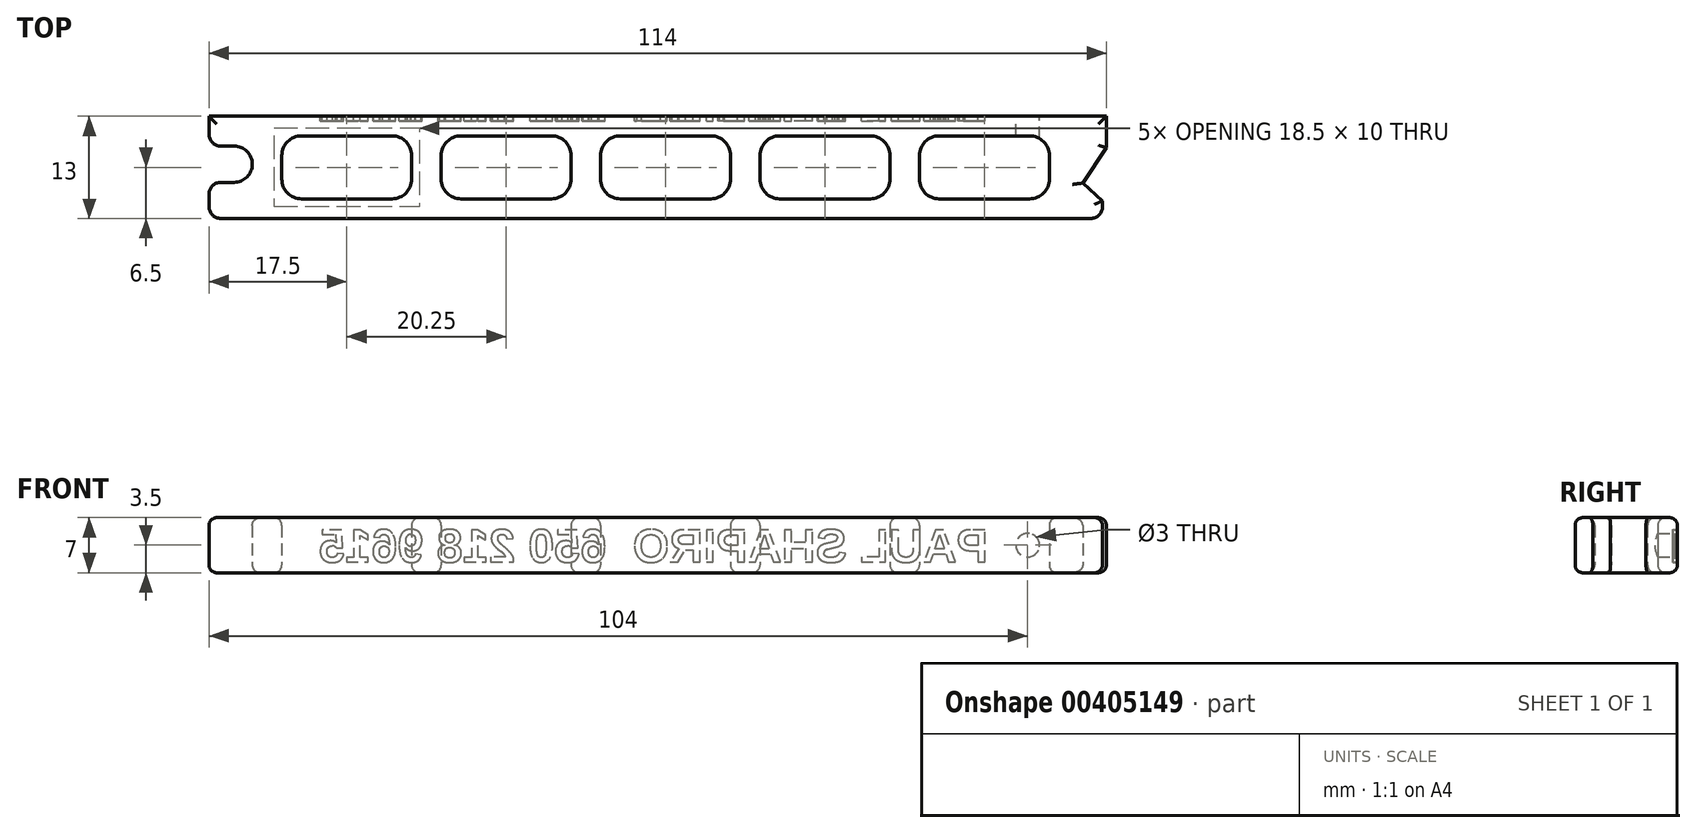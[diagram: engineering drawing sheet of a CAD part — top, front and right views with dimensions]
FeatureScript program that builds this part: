
annotation { "Feature Type Name" : "Feature", "Feature Type Description" : "" }
export const myFeature = defineFeature(function(context is Context, id is Id, definition is map)
    precondition{}
    {
        {
            var Q0;
            Q0=qCreatedBy(makeId("Top.planeOp"),FACE);
            var sketch = newSketch(context, id + "F0", { "sketchPlane" : qUnion([Q0])});
            skLineSegment(sketch, "E0.bottom", {"start": v(1.5, 0) * mm, "end": v(112, 0) * mm});
            skLineSegment(sketch, "E0.top", {"start": v(0, 13) * mm, "end": v(114, 13) * mm});
            skLineSegment(sketch, "E1", {"start": v(0, 13) * mm, "end": v(0, 10.7) * mm});
            skLineSegment(sketch, "E2.bottom", {"start": v(1.5, 4.6) * mm, "end": v(3.2, 4.6) * mm});
            skLineSegment(sketch, "E2.top", {"start": v(1.5, 9.2) * mm, "end": v(3.2, 9.2) * mm});
            skArc(sketch, "E3", {"start": v(3.2, 4.6) * mm, "mid": v(5.5, 6.9) * mm, "end": v(3.2, 9.2) * mm});
            skLineSegment(sketch, "E4.trimOffspring", {"start": v(0, 3.1) * mm, "end": v(0, 1.5) * mm});
            skLineSegment(sketch, "E5", {"start": v(0, 9.2) * mm, "end": v(0, 4.6) * mm, "construction": true});
            skLineSegment(sketch, "E6", {"start": v(0, 6.9) * mm, "end": v(3.2, 6.9) * mm, "construction": true});
            skLineSegment(sketch, "E7", {"start": v(114, 13) * mm, "end": v(114, 9) * mm});
            skPoint(sketch, "E8.visualSharp", {"position": v(0, 0) * mm});
            skArc(sketch, "E8.filletArc", {"start": v(0, 1.5) * mm, "mid": v(0.44, 0.44) * mm, "end": v(1.5, 0) * mm});
            skPoint(sketch, "E9.visualSharp", {"position": v(0, 4.6) * mm});
            skArc(sketch, "E9.filletArc", {"start": v(1.5, 4.6) * mm, "mid": v(0.44, 4.16) * mm, "end": v(0, 3.1) * mm});
            skPoint(sketch, "E10.visualSharp", {"position": v(0, 9.2) * mm});
            skArc(sketch, "E10.filletArc", {"start": v(0, 10.7) * mm, "mid": v(0.44, 9.64) * mm, "end": v(1.5, 9.2) * mm});
            skPoint(sketch, "E11.visualSharp", {"position": v(114, 4.5) * mm});
            skLineSegment(sketch, "E12", {"start": v(114, 4.5) * mm, "end": v(111, 4.5) * mm, "construction": true});
            skLineSegment(sketch, "E13", {"start": v(114, 9) * mm, "end": v(111, 4.5) * mm});
            skLineSegment(sketch, "E14", {"start": v(113.5, 2.25) * mm, "end": v(111, 4.5) * mm});
            skArc(sketch, "E15", {"start": v(112, 0) * mm, "mid": v(113.06, 0.44) * mm, "end": v(113.5, 1.5) * mm});
            skLineSegment(sketch, "E16", {"start": v(112, 1.5) * mm, "end": v(114.8, 1.5) * mm, "construction": true});
            skLineSegment(sketch, "E17", {"start": v(113.5, 2.25) * mm, "end": v(113.5, 1.5) * mm});
            skSolve(sketch);
        }
        {
            var Q0;
            Q0=makeQuery(id+"F0.imprint","IMPRINT",FACE,{"disambiguationData":[TD([[makeQuery(id+"F0.imprint","IMPRINT",EDGE,{"derivedFrom":sQuery(id+"F0.wireOp",EDGE,"E0.bottom")}),1.0]])]});
            extrude(context, id + "F1", {"entities" : qUnion([Q0]), "depth" : 7 * mm});
        }
        {
            var Q0;
            Q0=makeQuery(id+"F1.opExtrude","CAP_FACE",FACE,{"disambiguationData":[OSD([sQuery(id+"F0.wireOp",EDGE,"E0.bottom"),sQuery(id+"F0.wireOp",EDGE,"E0.top"),sQuery(id+"F0.wireOp",EDGE,"E1"),sQuery(id+"F0.wireOp",EDGE,"E2.bottom"),sQuery(id+"F0.wireOp",EDGE,"E2.top"),sQuery(id+"F0.wireOp",EDGE,"E3"),sQuery(id+"F0.wireOp",EDGE,"E4.trimOffspring"),sQuery(id+"F0.wireOp",EDGE,"E7"),sQuery(id+"F0.wireOp",EDGE,"c30ca287-96d4-4dfe-8688-3bdeec023004"),sQuery(id+"F0.wireOp",EDGE,"f645941c-dc99-4dda-a8e2-c4b280260802"),sQuery(id+"F0.wireOp",EDGE,"a89c6d0d-95b4-4aa5-8d05-a083aa38cfd4")])],"isStart":true});
            var sketch = newSketch(context, id + "F2", { "sketchPlane" : qUnion([Q0])});
            skLineSegment(sketch, "E18.bottom", {"start": v(104.25, -2.5) * mm, "end": v(92.75, -2.5) * mm});
            skLineSegment(sketch, "E18.top", {"start": v(104.25, -10.5) * mm, "end": v(92.75, -10.5) * mm});
            skLineSegment(sketch, "E18.left", {"start": v(106.75, -5) * mm, "end": v(106.75, -8) * mm});
            skLineSegment(sketch, "E18.right", {"start": v(90.25, -5) * mm, "end": v(90.25, -8) * mm});
            skLineSegment(sketch, "E19", {"start": v(106.75, -10.5) * mm, "end": v(106.75, -13) * mm, "construction": true});
            skLineSegment(sketch, "E20", {"start": v(106.75, -2.5) * mm, "end": v(106.75, 0) * mm, "construction": true});
            skPoint(sketch, "E21.visualSharp", {"position": v(90.25, -10.5) * mm});
            skArc(sketch, "E21.filletArc", {"start": v(90.25, -8) * mm, "mid": v(90.98, -9.77) * mm, "end": v(92.75, -10.5) * mm});
            skPoint(sketch, "E22.visualSharp", {"position": v(90.25, -2.5) * mm});
            skArc(sketch, "E22.filletArc", {"start": v(92.75, -2.5) * mm, "mid": v(90.98, -3.23) * mm, "end": v(90.25, -5) * mm});
            skPoint(sketch, "E23.visualSharp", {"position": v(106.75, -2.5) * mm});
            skArc(sketch, "E23.filletArc", {"start": v(106.75, -5) * mm, "mid": v(106.02, -3.23) * mm, "end": v(104.25, -2.5) * mm});
            skPoint(sketch, "E24.visualSharp", {"position": v(106.75, -10.5) * mm});
            skArc(sketch, "E24.filletArc", {"start": v(104.25, -10.5) * mm, "mid": v(106.02, -9.77) * mm, "end": v(106.75, -8) * mm});
            skLineSegment(sketch, "E25.1.0.0", {"start": v(84, -2.5) * mm, "end": v(72.5, -2.5) * mm});
            skPoint(sketch, "E25.1.0.1", {"position": v(86.5, -2.5) * mm});
            skLineSegment(sketch, "E25.1.0.2", {"start": v(84, -10.5) * mm, "end": v(72.5, -10.5) * mm});
            skPoint(sketch, "E25.1.0.3", {"position": v(86.5, -10.5) * mm});
            skLineSegment(sketch, "E25.1.0.4", {"start": v(70, -5) * mm, "end": v(70, -8) * mm});
            skLineSegment(sketch, "E25.1.0.5", {"start": v(86.5, -5) * mm, "end": v(86.5, -8) * mm});
            skPoint(sketch, "E25.1.0.6", {"position": v(70, -2.5) * mm});
            skPoint(sketch, "E25.1.0.7", {"position": v(70, -10.5) * mm});
            skArc(sketch, "E25.1.0.8", {"start": v(72.5, -2.5) * mm, "mid": v(70.73, -3.23) * mm, "end": v(70, -5) * mm});
            skArc(sketch, "E25.1.0.9", {"start": v(70, -8) * mm, "mid": v(70.73, -9.77) * mm, "end": v(72.5, -10.5) * mm});
            skArc(sketch, "E25.1.0.10", {"start": v(86.5, -5) * mm, "mid": v(85.77, -3.23) * mm, "end": v(84, -2.5) * mm});
            skArc(sketch, "E25.1.0.11", {"start": v(84, -10.5) * mm, "mid": v(85.77, -9.77) * mm, "end": v(86.5, -8) * mm});
            skLineSegment(sketch, "E25.2.0.0", {"start": v(63.75, -2.5) * mm, "end": v(52.25, -2.5) * mm});
            skPoint(sketch, "E25.2.0.1", {"position": v(66.25, -2.5) * mm});
            skLineSegment(sketch, "E25.2.0.2", {"start": v(63.75, -10.5) * mm, "end": v(52.25, -10.5) * mm});
            skPoint(sketch, "E25.2.0.3", {"position": v(66.25, -10.5) * mm});
            skLineSegment(sketch, "E25.2.0.4", {"start": v(49.75, -5) * mm, "end": v(49.75, -8) * mm});
            skLineSegment(sketch, "E25.2.0.5", {"start": v(66.25, -5) * mm, "end": v(66.25, -8) * mm});
            skPoint(sketch, "E25.2.0.6", {"position": v(49.75, -2.5) * mm});
            skPoint(sketch, "E25.2.0.7", {"position": v(49.75, -10.5) * mm});
            skArc(sketch, "E25.2.0.8", {"start": v(52.25, -2.5) * mm, "mid": v(50.48, -3.23) * mm, "end": v(49.75, -5) * mm});
            skArc(sketch, "E25.2.0.9", {"start": v(49.75, -8) * mm, "mid": v(50.48, -9.77) * mm, "end": v(52.25, -10.5) * mm});
            skArc(sketch, "E25.2.0.10", {"start": v(66.25, -5) * mm, "mid": v(65.52, -3.23) * mm, "end": v(63.75, -2.5) * mm});
            skArc(sketch, "E25.2.0.11", {"start": v(63.75, -10.5) * mm, "mid": v(65.52, -9.77) * mm, "end": v(66.25, -8) * mm});
            skLineSegment(sketch, "E25.3.0.0", {"start": v(43.5, -2.5) * mm, "end": v(32, -2.5) * mm});
            skPoint(sketch, "E25.3.0.1", {"position": v(46, -2.5) * mm});
            skLineSegment(sketch, "E25.3.0.2", {"start": v(43.5, -10.5) * mm, "end": v(32, -10.5) * mm});
            skPoint(sketch, "E25.3.0.3", {"position": v(46, -10.5) * mm});
            skLineSegment(sketch, "E25.3.0.4", {"start": v(29.5, -5) * mm, "end": v(29.5, -8) * mm});
            skLineSegment(sketch, "E25.3.0.5", {"start": v(46, -5) * mm, "end": v(46, -8) * mm});
            skPoint(sketch, "E25.3.0.6", {"position": v(29.5, -2.5) * mm});
            skPoint(sketch, "E25.3.0.7", {"position": v(29.5, -10.5) * mm});
            skArc(sketch, "E25.3.0.8", {"start": v(32, -2.5) * mm, "mid": v(30.23, -3.23) * mm, "end": v(29.5, -5) * mm});
            skArc(sketch, "E25.3.0.9", {"start": v(29.5, -8) * mm, "mid": v(30.23, -9.77) * mm, "end": v(32, -10.5) * mm});
            skArc(sketch, "E25.3.0.10", {"start": v(46, -5) * mm, "mid": v(45.27, -3.23) * mm, "end": v(43.5, -2.5) * mm});
            skArc(sketch, "E25.3.0.11", {"start": v(43.5, -10.5) * mm, "mid": v(45.27, -9.77) * mm, "end": v(46, -8) * mm});
            skLineSegment(sketch, "E25.4.0.0", {"start": v(23.25, -2.5) * mm, "end": v(11.75, -2.5) * mm});
            skPoint(sketch, "E25.4.0.1", {"position": v(25.75, -2.5) * mm});
            skLineSegment(sketch, "E25.4.0.2", {"start": v(23.25, -10.5) * mm, "end": v(11.75, -10.5) * mm});
            skPoint(sketch, "E25.4.0.3", {"position": v(25.75, -10.5) * mm});
            skLineSegment(sketch, "E25.4.0.4", {"start": v(9.25, -5) * mm, "end": v(9.25, -8) * mm});
            skLineSegment(sketch, "E25.4.0.5", {"start": v(25.75, -5) * mm, "end": v(25.75, -8) * mm});
            skPoint(sketch, "E25.4.0.6", {"position": v(9.25, -2.5) * mm});
            skPoint(sketch, "E25.4.0.7", {"position": v(9.25, -10.5) * mm});
            skArc(sketch, "E25.4.0.8", {"start": v(11.75, -2.5) * mm, "mid": v(9.98, -3.23) * mm, "end": v(9.25, -5) * mm});
            skArc(sketch, "E25.4.0.9", {"start": v(9.25, -8) * mm, "mid": v(9.98, -9.77) * mm, "end": v(11.75, -10.5) * mm});
            skArc(sketch, "E25.4.0.10", {"start": v(25.75, -5) * mm, "mid": v(25.02, -3.23) * mm, "end": v(23.25, -2.5) * mm});
            skArc(sketch, "E25.4.0.11", {"start": v(23.25, -10.5) * mm, "mid": v(25.02, -9.77) * mm, "end": v(25.75, -8) * mm});
            skLineSegment(sketch, "E25.direction1", {"start": v(92.75, -2.5) * mm, "end": v(72.5, -2.5) * mm, "construction": true});
            skSolve(sketch);
        }
        {
            var Q0;
            Q0=qSketchRegion(id+"F2",true);
            extrude(context, id + "F3", {"entities" : qUnion([Q0]), "operationType" : NewBodyOperationType.REMOVE, "endBound" : BoundingType.THROUGH_ALL, "oppositeDirection" : true, "depth" : 13.73 * mm});
        }
        {
            var Q0;
            Q0=makeQuery(id+"F1.opExtrude","CAP_FACE",FACE,{"disambiguationData":[OSD([sQuery(id+"F0.wireOp",EDGE,"E0.bottom"),sQuery(id+"F0.wireOp",EDGE,"E0.top"),sQuery(id+"F0.wireOp",EDGE,"E1"),sQuery(id+"F0.wireOp",EDGE,"E2.bottom"),sQuery(id+"F0.wireOp",EDGE,"E2.top"),sQuery(id+"F0.wireOp",EDGE,"E3"),sQuery(id+"F0.wireOp",EDGE,"E4.trimOffspring"),sQuery(id+"F0.wireOp",EDGE,"E7"),sQuery(id+"F0.wireOp",EDGE,"a89c6d0d-95b4-4aa5-8d05-a083aa38cfd4"),sQuery(id+"F0.wireOp",EDGE,"843786d9-8344-4bf4-b63c-bd20b21d23d6.filletArc"),sQuery(id+"F0.wireOp",EDGE,"E8.filletArc"),sQuery(id+"F0.wireOp",EDGE,"E9.filletArc"),sQuery(id+"F0.wireOp",EDGE,"E10.filletArc"),sQuery(id+"F0.wireOp",EDGE,"E13"),sQuery(id+"F0.wireOp",EDGE,"34148787-0765-4789-8ede-2cb2b04cca70")])],"isStart":true});
            var Q1;
            Q1=makeQuery(id+"F1.opExtrude","CAP_FACE",FACE,{"disambiguationData":[OSD([sQuery(id+"F0.wireOp",EDGE,"E0.bottom"),sQuery(id+"F0.wireOp",EDGE,"E0.top"),sQuery(id+"F0.wireOp",EDGE,"E1"),sQuery(id+"F0.wireOp",EDGE,"E2.bottom"),sQuery(id+"F0.wireOp",EDGE,"E2.top"),sQuery(id+"F0.wireOp",EDGE,"E3"),sQuery(id+"F0.wireOp",EDGE,"E4.trimOffspring"),sQuery(id+"F0.wireOp",EDGE,"E7"),sQuery(id+"F0.wireOp",EDGE,"a89c6d0d-95b4-4aa5-8d05-a083aa38cfd4"),sQuery(id+"F0.wireOp",EDGE,"843786d9-8344-4bf4-b63c-bd20b21d23d6.filletArc"),sQuery(id+"F0.wireOp",EDGE,"E8.filletArc"),sQuery(id+"F0.wireOp",EDGE,"E9.filletArc"),sQuery(id+"F0.wireOp",EDGE,"E10.filletArc"),sQuery(id+"F0.wireOp",EDGE,"E13"),sQuery(id+"F0.wireOp",EDGE,"34148787-0765-4789-8ede-2cb2b04cca70")])],"isStart":false});
            fillet(context, id + "F4", {"entities" : qUnion([Q0, Q1]), "radius" : 1 * mm, "allowEdgeOverflow" : false});
        }
        {
            var Q0;
            Q0=makeQuery(id+"F1.opExtrude","SWEPT_FACE",FACE,{"disambiguationData":[OSD([sQuery(id+"F0.wireOp",EDGE,"E0.top")])]});
            var sketch = newSketch(context, id + "F5", { "sketchPlane" : qUnion([Q0])});
            skLineSegment(sketch, "E26", {"start": v(-104, 1) * mm, "end": v(-104, 6) * mm, "construction": true});
            skCircle(sketch, "E27", {"center": v(-104, 3.5) * mm, "radius": 1.5 * mm});
            skSolve(sketch);
        }
        {
            var Q0;
            Q0=makeQuery(id+"F5.imprint","IMPRINT",FACE,{"disambiguationData":[TD([[makeQuery(id+"F5.imprint","IMPRINT",EDGE,{"derivedFrom":sQuery(id+"F5.wireOp",EDGE,"E27")}),1.0]])]});
            extrude(context, id + "F6", {"entities" : qUnion([Q0]), "operationType" : NewBodyOperationType.REMOVE, "endBound" : BoundingType.UP_TO_NEXT, "oppositeDirection" : true, "depth" : 25 * mm});
        }
        {
            var Q0;
            Q0=makeQuery(id+"F1.opExtrude","SWEPT_FACE",FACE,{"disambiguationData":[OSD([sQuery(id+"F0.wireOp",EDGE,"E0.top")])]});
            var sketch = newSketch(context, id + "F7", { "sketchPlane" : qUnion([Q0])});
            skText(sketch, "E28", { "text": "PAUL SHAPIRO  650 218 9615", "fontName": "Arimo-Bold.ttf"});
            skLineSegment(sketch, "E29", {"start": v(-98.95, 5.65) * mm, "end": v(-98.95, 6) * mm, "construction": true});
            skLineSegment(sketch, "E30", {"start": v(-98.95, 1.35) * mm, "end": v(-98.95, 1) * mm, "construction": true});
            const initialGuessF7  = {"E28": [-0.09895, 0.00135, 1, 0, 0.0043]};
            skSetInitialGuess(sketch, initialGuessF7);
            skSolve(sketch);
        }
        {
            var Q0;
            Q0=qSketchRegion(id+"F7",true);
            extrude(context, id + "F8", {"entities" : qUnion([Q0]), "operationType" : NewBodyOperationType.REMOVE, "oppositeDirection" : true, "depth" : .6 * mm});
        }
    });
